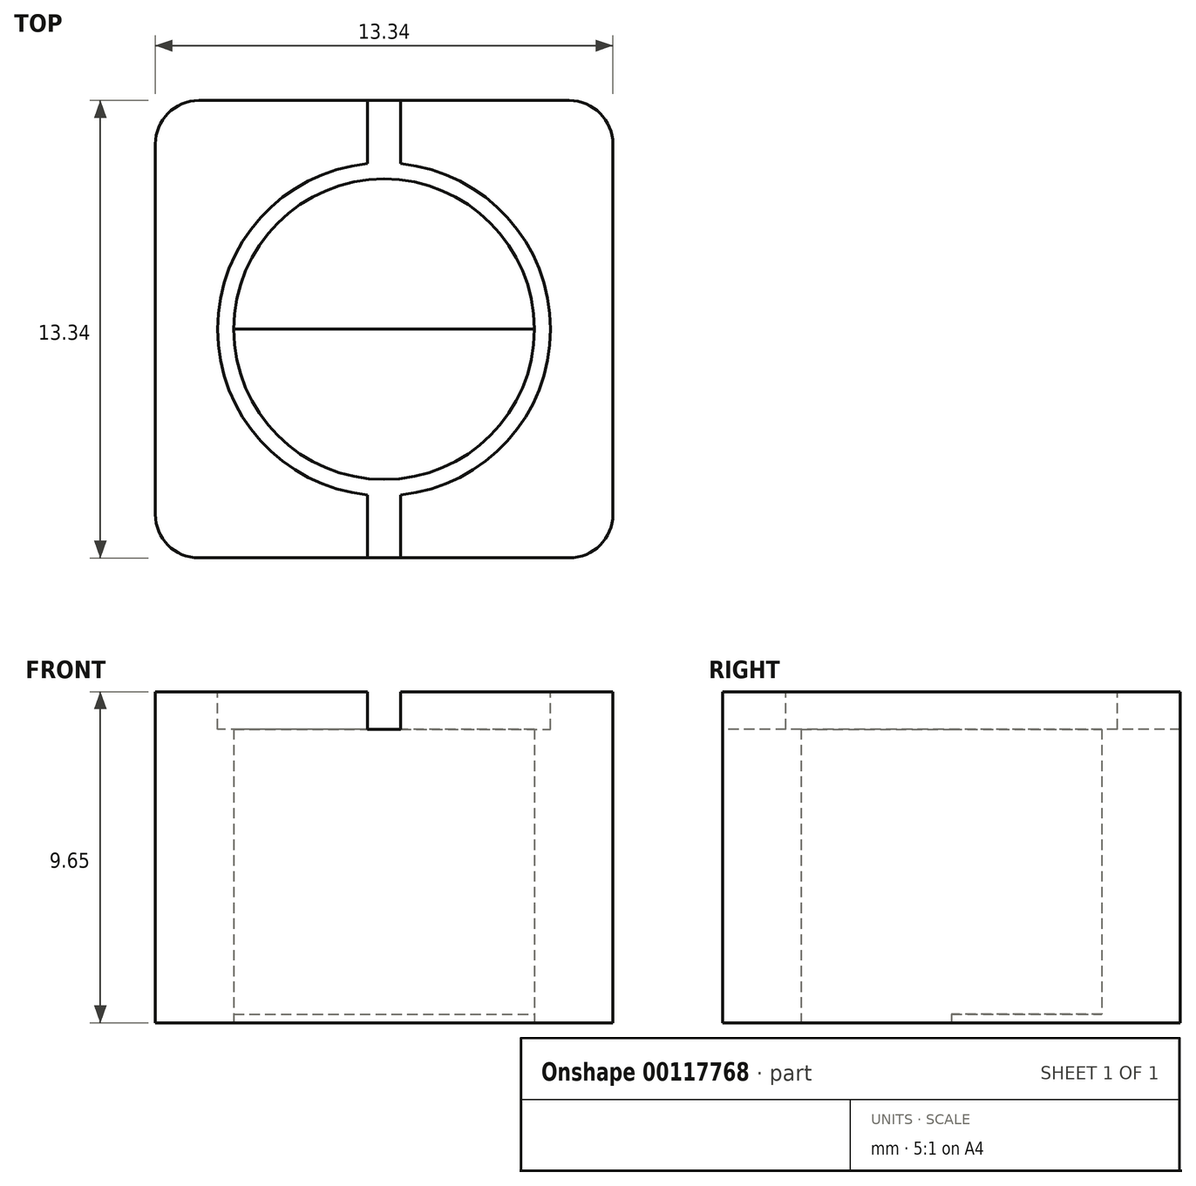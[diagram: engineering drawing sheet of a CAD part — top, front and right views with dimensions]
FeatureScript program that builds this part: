
annotation { "Feature Type Name" : "Feature", "Feature Type Description" : "" }
export const myFeature = defineFeature(function(context is Context, id is Id, definition is map)
    precondition{}
    {
        {
            var Q0;
            Q0=qCreatedBy(makeId("Top.planeOp"),FACE);
            var sketch = newSketch(context, id + "F0", { "sketchPlane" : qUnion([Q0])});
            skLineSegment(sketch, "E0.bottom", {"start": v(6.67, 6.67) * mm, "end": v(-6.67, 6.67) * mm});
            skLineSegment(sketch, "E0.top", {"start": v(6.67, -6.67) * mm, "end": v(-6.67, -6.67) * mm});
            skLineSegment(sketch, "E0.left", {"start": v(6.67, 6.67) * mm, "end": v(6.67, -6.67) * mm});
            skLineSegment(sketch, "E0.right", {"start": v(-6.67, 6.67) * mm, "end": v(-6.67, -6.67) * mm});
            skPoint(sketch, "E0.middle", {"position": v(0, 0) * mm});
            skCircle(sketch, "E1", {"center": v(0, 0) * mm, "radius": 4.38 * mm});
            skSolve(sketch);
        }
        {
            var Q0;
            Q0 = qSketchRegion(id + "F0", true);
            extrude(context, id + "F1", {"entities" : qUnion([Q0]), "depth" : 9.65 * mm});
        }
        {
            var Q0;
            Q0=makeQuery(id+"F1.opExtrude","CAP_FACE",FACE,{"disambiguationData":[OSD([sQuery(id+"F0.wireOp",EDGE,"E0.bottom"),sQuery(id+"F0.wireOp",EDGE,"E0.top"),sQuery(id+"F0.wireOp",EDGE,"E0.left"),sQuery(id+"F0.wireOp",EDGE,"E0.right"),sQuery(id+"F0.wireOp",EDGE,"E1")])],"isStart":false});
            var sketch = newSketch(context, id + "F2", { "sketchPlane" : qUnion([Q0])});
            skLineSegment(sketch, "E2.bottom", {"start": v(0.48, 6.67) * mm, "end": v(-0.48, 6.67) * mm});
            skLineSegment(sketch, "E2.top", {"start": v(0.48, -6.67) * mm, "end": v(-0.48, -6.67) * mm});
            skLineSegment(sketch, "E2.left", {"start": v(0.48, 6.67) * mm, "end": v(0.48, -6.67) * mm});
            skLineSegment(sketch, "E2.right", {"start": v(-0.48, 6.67) * mm, "end": v(-0.48, -6.67) * mm});
            skPoint(sketch, "E2.middle", {"position": v(0, 0) * mm});
            skSolve(sketch);
        }
        {
            var Q0;
            Q0 = qSketchRegion(id + "F2", true);
            extrude(context, id + "F3", {"entities" : qUnion([Q0]), "operationType" : NewBodyOperationType.REMOVE, "oppositeDirection" : true, "offsetDistance" : 25 * mm, "depth" : 1.1 * mm});
        }
        {
            var Q0;
            Q0=makeQuery(id+"F1.opExtrude","SWEPT_EDGE",EDGE,{"disambiguationData":[OSD([sQuery(id+"F0.wireOp",EDGE,"E0.top"),sQuery(id+"F0.wireOp",EDGE,"E0.right")])]});
            var Q1;
            Q1=makeQuery(id+"F1.opExtrude","SWEPT_EDGE",EDGE,{"disambiguationData":[OSD([sQuery(id+"F0.wireOp",EDGE,"E0.top"),sQuery(id+"F0.wireOp",EDGE,"E0.left")])]});
            var Q2;
            Q2=makeQuery(id+"F1.opExtrude","SWEPT_EDGE",EDGE,{"disambiguationData":[OSD([sQuery(id+"F0.wireOp",EDGE,"E0.bottom"),sQuery(id+"F0.wireOp",EDGE,"E0.left")])]});
            var Q3;
            Q3=makeQuery(id+"F1.opExtrude","SWEPT_EDGE",EDGE,{"disambiguationData":[OSD([sQuery(id+"F0.wireOp",EDGE,"E0.bottom"),sQuery(id+"F0.wireOp",EDGE,"E0.right")])]});
            fillet(context, id + "F4", {"entities" : qUnion([Q0, Q1, Q2, Q3]), "radius" : 1.27 * mm, "tangentPropagation" : true, "allowEdgeOverflow" : false});
        }
        {
            var Q0;
            {var subQ0=sQuery(id+"F0.wireOp",EDGE,"E1");var subQ1=sQuery(id+"F0.wireOp",EDGE,"E0.right");var subQ2=sQuery(id+"F0.wireOp",EDGE,"E0.top");var subQ3=sQuery(id+"F0.wireOp",EDGE,"E0.bottom");Q0=makeQuery(id+"F3.boolean.opBoolean","SPLIT",FACE,{"disambiguationData":[TD([makeQuery(id+"F1.opExtrude","SWEPT_FACE",FACE,{"disambiguationData":[OSD([subQ1])]})])],"derivedFrom":makeQuery(id+"F1.opExtrude","CAP_FACE",FACE,{"disambiguationData":[OSD([subQ3,subQ2,sQuery(id+"F0.wireOp",EDGE,"E0.left"),subQ1,subQ0])],"isStart":false})});}
            var sketch = newSketch(context, id + "F5", { "sketchPlane" : qUnion([Q0])});
            skCircle(sketch, "E3", {"center": v(0, 0) * mm, "radius": 4.85 * mm});
            skSolve(sketch);
        }
        {
            var Q0;
            Q0 = qSketchRegion(id + "F5", true);
            extrude(context, id + "F6", {"entities" : qUnion([Q0]), "operationType" : NewBodyOperationType.REMOVE, "oppositeDirection" : true, "offsetDistance" : 25 * mm, "depth" : 1.1 * mm});
        }
        {
            var Q0;
            Q0=makeQuery(id+"F1.opExtrude","CAP_FACE",FACE,{"disambiguationData":[OSD([sQuery(id+"F0.wireOp",EDGE,"E0.bottom"),sQuery(id+"F0.wireOp",EDGE,"E0.top"),sQuery(id+"F0.wireOp",EDGE,"E0.left"),sQuery(id+"F0.wireOp",EDGE,"E0.right"),sQuery(id+"F0.wireOp",EDGE,"E1")])],"isStart":true});
            var sketch = newSketch(context, id + "F7", { "sketchPlane" : qUnion([Q0])});
            skLineSegment(sketch, "E4.bottom", {"start": v(-6.67, 0) * mm, "end": v(6.67, 0) * mm});
            skLineSegment(sketch, "E4.top", {"start": v(-6.67, -4.87) * mm, "end": v(6.67, -4.87) * mm});
            skLineSegment(sketch, "E4.left", {"start": v(-6.67, 0) * mm, "end": v(-6.67, -4.87) * mm});
            skLineSegment(sketch, "E4.right", {"start": v(6.67, 0) * mm, "end": v(6.67, -4.87) * mm});
            skSolve(sketch);
        }
        {
            var Q0;
            Q0 = qSketchRegion(id + "F7", true);
            extrude(context, id + "F8", {"entities" : qUnion([Q0]), "operationType" : NewBodyOperationType.ADD, "oppositeDirection" : true, "depth" : 0.25 * mm});
        }
    });
